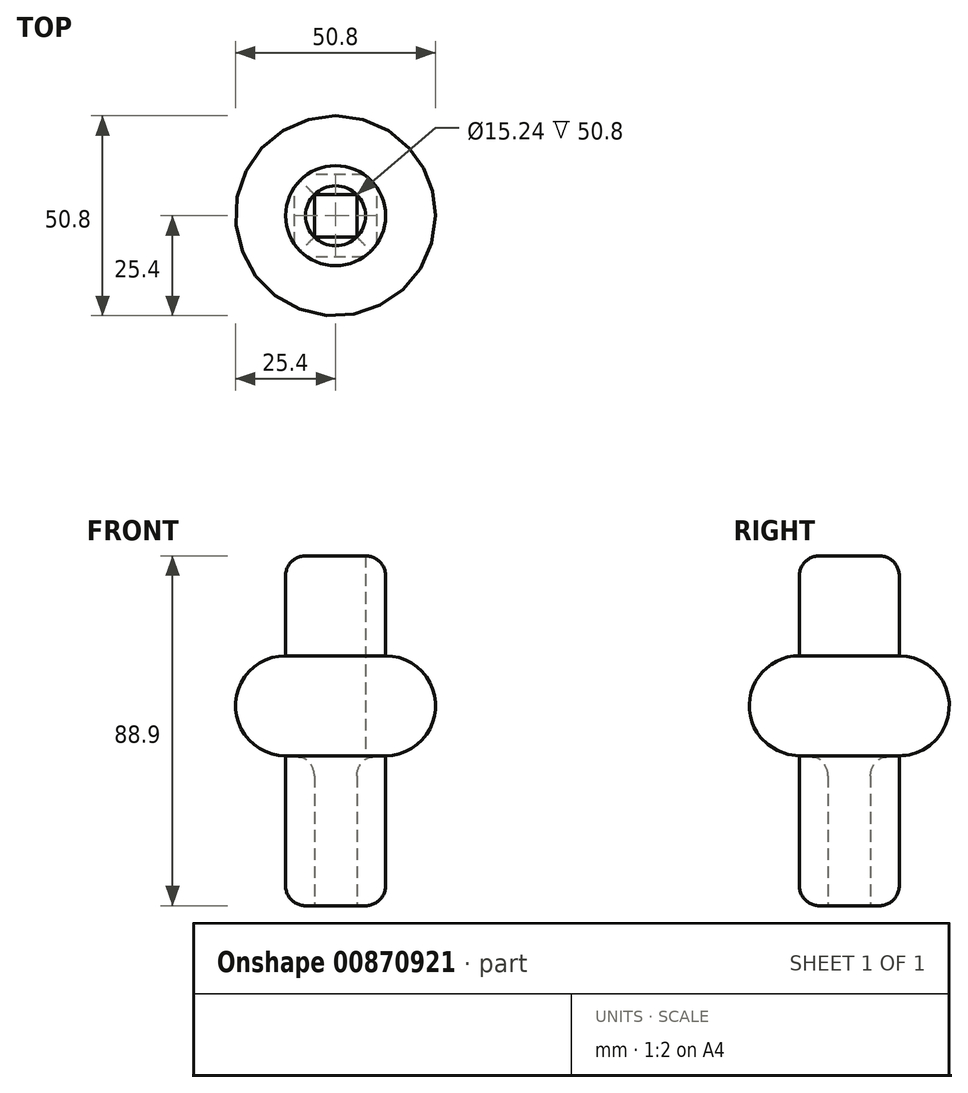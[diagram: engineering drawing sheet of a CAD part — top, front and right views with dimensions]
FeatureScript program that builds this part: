
annotation { "Feature Type Name" : "Feature", "Feature Type Description" : "" }
export const myFeature = defineFeature(function(context is Context, id is Id, definition is map)
    precondition{}
    {
        {
            var Q0;
            Q0=qCreatedBy(makeId("Top.planeOp"),FACE);
            var sketch = newSketch(context, id + "F0", { "sketchPlane" : qUnion([Q0])});
            skCircle(sketch, "E0", {"center": v(0, 0) * mm, "radius": 12.7 * mm});
            skCircle(sketch, "E1", {"center": v(0, 0) * mm, "radius": 7.62 * mm});
            skLineSegment(sketch, "E2.bottom", {"start": v(5.39, -5.39) * mm, "end": v(-5.39, -5.39) * mm});
            skLineSegment(sketch, "E2.top", {"start": v(5.39, 5.39) * mm, "end": v(-5.39, 5.39) * mm});
            skLineSegment(sketch, "E2.left", {"start": v(5.39, -5.39) * mm, "end": v(5.39, 5.39) * mm});
            skLineSegment(sketch, "E2.right", {"start": v(-5.39, -5.39) * mm, "end": v(-5.39, 5.39) * mm});
            skSolve(sketch);
        }
        {
            var Q0;
            Q0=makeQuery(id+"F0.imprint","IMPRINT",FACE,{"disambiguationData":[TD([[makeQuery(id+"F0.imprint","IMPRINT",EDGE,{"derivedFrom":sQuery(id+"F0.wireOp",EDGE,"E0")}),1.0]])]});
            var Q1;
            {var subQ0=sQuery(id+"F0.wireOp",EDGE,"E2.bottom");Q1=makeQuery(id+"F0.imprint","IMPRINT",FACE,{"disambiguationData":[TD([[makeQuery(id+"F0.imprint","IMPRINT",EDGE,{"derivedFrom":subQ0}),1.0]])]});}
            var Q2;
            {var subQ0=sQuery(id+"F0.wireOp",EDGE,"E2.right");Q2=makeQuery(id+"F0.imprint","IMPRINT",FACE,{"disambiguationData":[TD([[makeQuery(id+"F0.imprint","IMPRINT",EDGE,{"derivedFrom":subQ0}),1.0]])]});}
            var Q3;
            {var subQ0=sQuery(id+"F0.wireOp",EDGE,"E2.left");Q3=makeQuery(id+"F0.imprint","IMPRINT",FACE,{"disambiguationData":[TD([[makeQuery(id+"F0.imprint","IMPRINT",EDGE,{"derivedFrom":subQ0}),-1.0]])]});}
            var Q4;
            {var subQ0=sQuery(id+"F0.wireOp",EDGE,"E2.top");Q4=makeQuery(id+"F0.imprint","IMPRINT",FACE,{"disambiguationData":[TD([[makeQuery(id+"F0.imprint","IMPRINT",EDGE,{"derivedFrom":subQ0}),-1.0]])]});}
            extrude(context, id + "F1", {"entities" : qUnion([Q0, Q1, Q2, Q3, Q4]), "depth" : 38.1 * mm, "offsetDistance" : 25.4 * mm});
        }
        {
            var Q0;
            Q0=makeQuery(id+"F1.opExtrude","CAP_FACE",FACE,{"disambiguationData":[OSD([sQuery(id+"F0.wireOp",EDGE,"E0"),sQuery(id+"F0.wireOp",EDGE,"E1")])],"isStart":false});
            var sketch = newSketch(context, id + "F2", { "sketchPlane" : qUnion([Q0])});
            skCircle(sketch, "E3", {"center": v(0, 0) * mm, "radius": 25.4 * mm});
            skSolve(sketch);
        }
        {
            var Q0;
            Q0=makeQuery(id+"F2.imprint","IMPRINT",FACE,{"disambiguationData":[TD([[makeQuery(id+"F2.imprint","IMPRINT",EDGE,{"derivedFrom":sQuery(id+"F2.wireOp",EDGE,"E3")}),1.0]])]});
            extrude(context, id + "F3", {"entities" : qUnion([Q0]), "depth" : 12.7 * mm, "offsetDistance" : 25.4 * mm});
        }
        {
            var Q0;
            Q0=makeQuery(id+"F3.opExtrude","CAP_EDGE",EDGE,{"disambiguationData":[OSD([sQuery(id+"F2.wireOp",EDGE,"E3")])],"isStart":true});
            fillet(context, id + "F4", {"entities" : qUnion([Q0]), "radius" : 12.7 * mm, "tangentPropagation" : true, "allowEdgeOverflow" : false});
        }
        {
            var Q0;
            Q0=makeQuery(id+"F1.opExtrude","CAP_EDGE",EDGE,{"disambiguationData":[OSD([sQuery(id+"F0.wireOp",EDGE,"E0")])],"isStart":true});
            fillet(context, id + "F5", {"entities" : qUnion([Q0]), "radius" : 5.08 * mm, "tangentPropagation" : true, "allowEdgeOverflow" : false});
        }
        {
            var Q0;
            Q0=makeQuery(id+"F1.opExtrude","CAP_EDGE",EDGE,{"disambiguationData":[OSD([sQuery(id+"F0.wireOp",EDGE,"E2.left")])],"isStart":false});
            var Q1;
            Q1=makeQuery(id+"F1.opExtrude","CAP_EDGE",EDGE,{"disambiguationData":[OSD([sQuery(id+"F0.wireOp",EDGE,"E2.bottom")])],"isStart":false});
            var Q2;
            Q2=makeQuery(id+"F1.opExtrude","CAP_EDGE",EDGE,{"disambiguationData":[OSD([sQuery(id+"F0.wireOp",EDGE,"E2.right")])],"isStart":false});
            var Q3;
            Q3=makeQuery(id+"F1.opExtrude","CAP_EDGE",EDGE,{"disambiguationData":[OSD([sQuery(id+"F0.wireOp",EDGE,"E2.top")])],"isStart":false});
            fillet(context, id + "F6", {"entities" : qUnion([Q0, Q1, Q2, Q3]), "radius" : 5.08 * mm, "tangentPropagation" : true, "allowEdgeOverflow" : false});
        }
        {
            var Q0;
            Q0=makeQuery(id+"F3.opExtrude","SWEPT_BODY",BODY,{"disambiguationData":[OSD([sQuery(id+"F0.wireOp",EDGE,"E0"),sQuery(id+"F2.wireOp",EDGE,"E3")])]});
            var Q1;
            Q1=makeQuery(id+"F3.opExtrude","CAP_FACE",FACE,{"disambiguationData":[OSD([sQuery(id+"F0.wireOp",EDGE,"E0"),sQuery(id+"F2.wireOp",EDGE,"E3")])],"isStart":false});
            mirror(context, id + "F7", {"operationType" : NewBodyOperationType.ADD, "entities" : qUnion([Q0]), "mirrorPlane" : qUnion([Q1])});
        }
        {
            var Q0;
            Q0=makeQuery(id+"F6.opFillet","SPLIT",FACE,{"disambiguationData":[OD(1.0)],"derivedFrom":makeQuery(id+"F1.opExtrude","CAP_FACE",FACE,{"disambiguationData":[OSD([sQuery(id+"F0.wireOp",EDGE,"E0"),sQuery(id+"F0.wireOp",EDGE,"E2.bottom"),sQuery(id+"F0.wireOp",EDGE,"E2.top"),sQuery(id+"F0.wireOp",EDGE,"E2.left"),sQuery(id+"F0.wireOp",EDGE,"E2.right")])],"isStart":false})});
            cPlane(context, id + "F8", {"entities" : qUnion([Q0]), "cplaneType" : CPlaneType.OFFSET, "offset" : 25.4 * mm, "width" : 152.4 * mm, "height" : 152.4 * mm});
        }
        {
            var Q0;
            Q0=qCreatedBy(id+"F8.planeOp",FACE);
            var sketch = newSketch(context, id + "F9", { "sketchPlane" : qUnion([Q0])});
            skCircle(sketch, "E4", {"center": v(0, 0) * mm, "radius": 12.7 * mm});
            skCircle(sketch, "E5", {"center": v(0, 0) * mm, "radius": 7.62 * mm});
            skSolve(sketch);
        }
        {
            var Q0;
            Q0=makeQuery(id+"F9.imprint","IMPRINT",FACE,{"disambiguationData":[TD([[makeQuery(id+"F9.imprint","IMPRINT",EDGE,{"derivedFrom":sQuery(id+"F9.wireOp",EDGE,"E4")}),1.0]])]});
            extrude(context, id + "F10", {"entities" : qUnion([Q0]), "depth" : 25.4 * mm, "offsetDistance" : 25.4 * mm});
        }
        {
            var Q0;
            Q0=makeQuery(id+"F10.opExtrude","CAP_EDGE",EDGE,{"disambiguationData":[OSD([sQuery(id+"F9.wireOp",EDGE,"E4")])],"isStart":false});
            fillet(context, id + "F11", {"entities" : qUnion([Q0]), "radius" : 5.08 * mm, "tangentPropagation" : true, "allowEdgeOverflow" : false});
        }
        {
            var Q0;
            Q0 = qSketchRegion(id + "F9", true);
            extrude(context, id + "F12", {"entities" : qUnion([Q0]), "operationType" : NewBodyOperationType.ADD, "oppositeDirection" : true, "depth" : 25.4 * mm, "offsetDistance" : 25.4 * mm});
        }
    });
